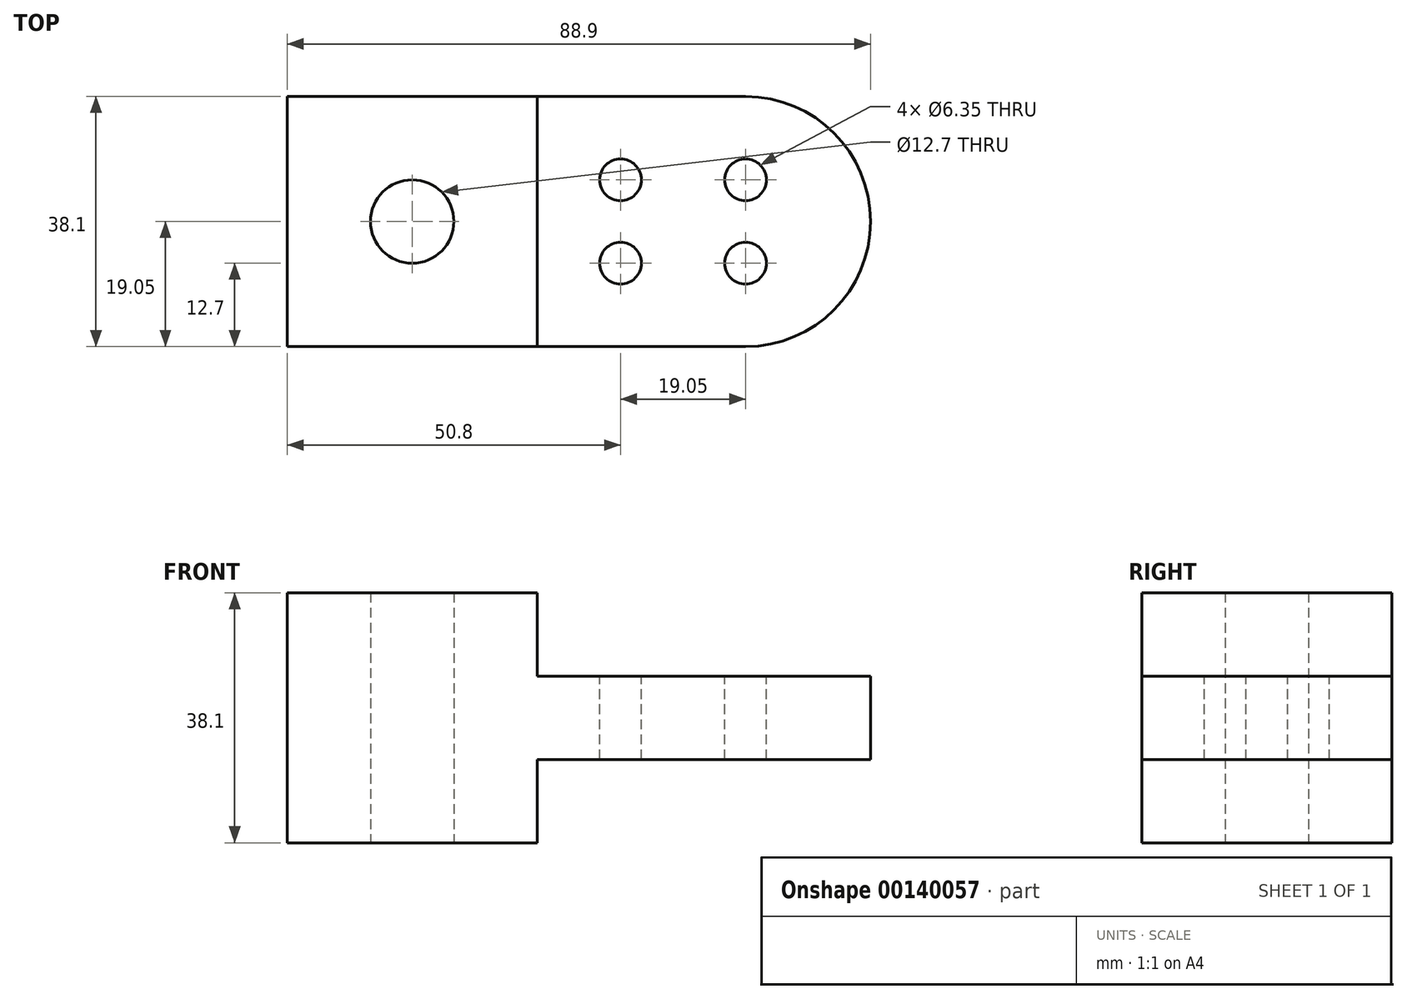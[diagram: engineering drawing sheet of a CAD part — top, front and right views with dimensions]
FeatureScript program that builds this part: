
annotation { "Feature Type Name" : "Feature", "Feature Type Description" : "" }
export const myFeature = defineFeature(function(context is Context, id is Id, definition is map)
    precondition{}
    {
        {
            var Q0;
            Q0=qCreatedBy(makeId("Top.planeOp"),FACE);
            var sketch = newSketch(context, id + "F0", { "sketchPlane" : qUnion([Q0])});
            skCircle(sketch, "E0", {"center": v(0, 0) * mm, "radius": 6.35 * mm});
            skLineSegment(sketch, "E1.bottom", {"start": v(-19.05, 19.05) * mm, "end": v(69.85, 19.05) * mm});
            skLineSegment(sketch, "E1.top", {"start": v(-19.05, -19.05) * mm, "end": v(69.85, -19.05) * mm});
            skLineSegment(sketch, "E1.left", {"start": v(-19.05, 19.05) * mm, "end": v(-19.05, -19.05) * mm});
            skLineSegment(sketch, "E1.right", {"start": v(69.85, 19.05) * mm, "end": v(69.85, -19.05) * mm});
            skSolve(sketch);
        }
        {
            var Q0;
            Q0 = qSketchRegion(id + "F0", true);
            extrude(context, id + "F1", {"entities" : qUnion([Q0]), "depth" : 38.1 * mm});
        }
        {
            var Q0;
            Q0=makeQuery(id+"F1.opExtrude","SWEPT_EDGE",EDGE,{"disambiguationData":[OSD([sQuery(id+"F0.wireOp",EDGE,"E1.bottom"),sQuery(id+"F0.wireOp",EDGE,"E1.right")])]});
            var Q1;
            Q1=makeQuery(id+"F1.opExtrude","SWEPT_EDGE",EDGE,{"disambiguationData":[OSD([sQuery(id+"F0.wireOp",EDGE,"E1.top"),sQuery(id+"F0.wireOp",EDGE,"E1.right")])]});
            fillet(context, id + "F2", {"entities" : qUnion([Q0, Q1]), "radius" : 19.05 * mm, "tangentPropagation" : true, "allowEdgeOverflow" : false});
        }
        {
            var Q0;
            Q0=makeQuery(id+"F1.opExtrude","SWEPT_FACE",FACE,{"disambiguationData":[OSD([sQuery(id+"F0.wireOp",EDGE,"E1.top")])]});
            var sketch = newSketch(context, id + "F3", { "sketchPlane" : qUnion([Q0])});
            skLineSegment(sketch, "E2.bottom", {"start": v(19.05, 38.1) * mm, "end": v(69.85, 38.1) * mm});
            skLineSegment(sketch, "E2.top", {"start": v(19.05, 25.4) * mm, "end": v(69.85, 25.4) * mm});
            skLineSegment(sketch, "E2.left", {"start": v(19.05, 38.1) * mm, "end": v(19.05, 25.4) * mm});
            skLineSegment(sketch, "E2.right", {"start": v(69.85, 38.1) * mm, "end": v(69.85, 25.4) * mm});
            skLineSegment(sketch, "E3.bottom", {"start": v(19.05, 0) * mm, "end": v(69.85, 0) * mm});
            skLineSegment(sketch, "E3.top", {"start": v(19.05, 12.7) * mm, "end": v(69.85, 12.7) * mm});
            skLineSegment(sketch, "E3.left", {"start": v(19.05, 0) * mm, "end": v(19.05, 12.7) * mm});
            skLineSegment(sketch, "E3.right", {"start": v(69.85, 0) * mm, "end": v(69.85, 12.7) * mm});
            skSolve(sketch);
        }
        {
            var Q0;
            {var subQ4=sQuery(id+"F3.wireOp",EDGE,"E2.left");Q0=makeQuery(id+"F3.imprint","IMPRINT",FACE,{"disambiguationData":[TD([[makeQuery(id+"F3.imprint","IMPRINT",EDGE,{"derivedFrom":subQ4}),1.0]])]});}
            var Q1;
            {var subQ4=sQuery(id+"F3.wireOp",EDGE,"E2.right");Q1=makeQuery(id+"F3.imprint","IMPRINT",FACE,{"disambiguationData":[TD([[makeQuery(id+"F3.imprint","IMPRINT",EDGE,{"derivedFrom":subQ4}),-1.0]])]});}
            var Q2;
            {var subQ4=sQuery(id+"F3.wireOp",EDGE,"E3.right");Q2=makeQuery(id+"F3.imprint","IMPRINT",FACE,{"disambiguationData":[TD([[makeQuery(id+"F3.imprint","IMPRINT",EDGE,{"derivedFrom":subQ4}),1.0]])]});}
            var Q3;
            {var subQ4=sQuery(id+"F3.wireOp",EDGE,"E3.left");Q3=makeQuery(id+"F3.imprint","IMPRINT",FACE,{"disambiguationData":[TD([[makeQuery(id+"F3.imprint","IMPRINT",EDGE,{"derivedFrom":subQ4}),-1.0]])]});}
            extrude(context, id + "F4", {"entities" : qUnion([Q0, Q1, Q2, Q3]), "operationType" : NewBodyOperationType.REMOVE, "endBound" : BoundingType.THROUGH_ALL, "oppositeDirection" : true, "depth" : 25.4 * mm});
        }
        {
            var Q0;
            Q0=makeQuery(id+"F4.boolean.opBoolean","COPY",FACE,{"derivedFrom":makeQuery(id+"F4.opExtrude","SWEPT_FACE",FACE,{"disambiguationData":[OSD([sQuery(id+"F3.wireOp",EDGE,"E2.top")])]})});
            var sketch = newSketch(context, id + "F5", { "sketchPlane" : qUnion([Q0])});
            skCircle(sketch, "E4", {"center": v(31.75, 6.35) * mm, "radius": 3.18 * mm});
            skCircle(sketch, "E5", {"center": v(50.8, 6.35) * mm, "radius": 3.18 * mm});
            skCircle(sketch, "E6", {"center": v(31.75, -6.35) * mm, "radius": 3.18 * mm});
            skCircle(sketch, "E7", {"center": v(50.8, -6.35) * mm, "radius": 3.18 * mm});
            skSolve(sketch);
        }
        {
            var Q0;
            Q0=makeQuery(id+"F5.imprint","IMPRINT",FACE,{"disambiguationData":[TD([[makeQuery(id+"F5.imprint","IMPRINT",EDGE,{"derivedFrom":sQuery(id+"F5.wireOp",EDGE,"E5")}),1.0]])]});
            var Q1;
            Q1=makeQuery(id+"F5.imprint","IMPRINT",FACE,{"disambiguationData":[TD([[makeQuery(id+"F5.imprint","IMPRINT",EDGE,{"derivedFrom":sQuery(id+"F5.wireOp",EDGE,"E7")}),1.0]])]});
            var Q2;
            Q2=makeQuery(id+"F5.imprint","IMPRINT",FACE,{"disambiguationData":[TD([[makeQuery(id+"F5.imprint","IMPRINT",EDGE,{"derivedFrom":sQuery(id+"F5.wireOp",EDGE,"E6")}),1.0]])]});
            var Q3;
            Q3=makeQuery(id+"F5.imprint","IMPRINT",FACE,{"disambiguationData":[TD([[makeQuery(id+"F5.imprint","IMPRINT",EDGE,{"derivedFrom":sQuery(id+"F5.wireOp",EDGE,"E4")}),1.0]])]});
            extrude(context, id + "F6", {"entities" : qUnion([Q0, Q1, Q2, Q3]), "operationType" : NewBodyOperationType.REMOVE, "endBound" : BoundingType.THROUGH_ALL, "oppositeDirection" : true, "depth" : 25.4 * mm});
        }
    });
